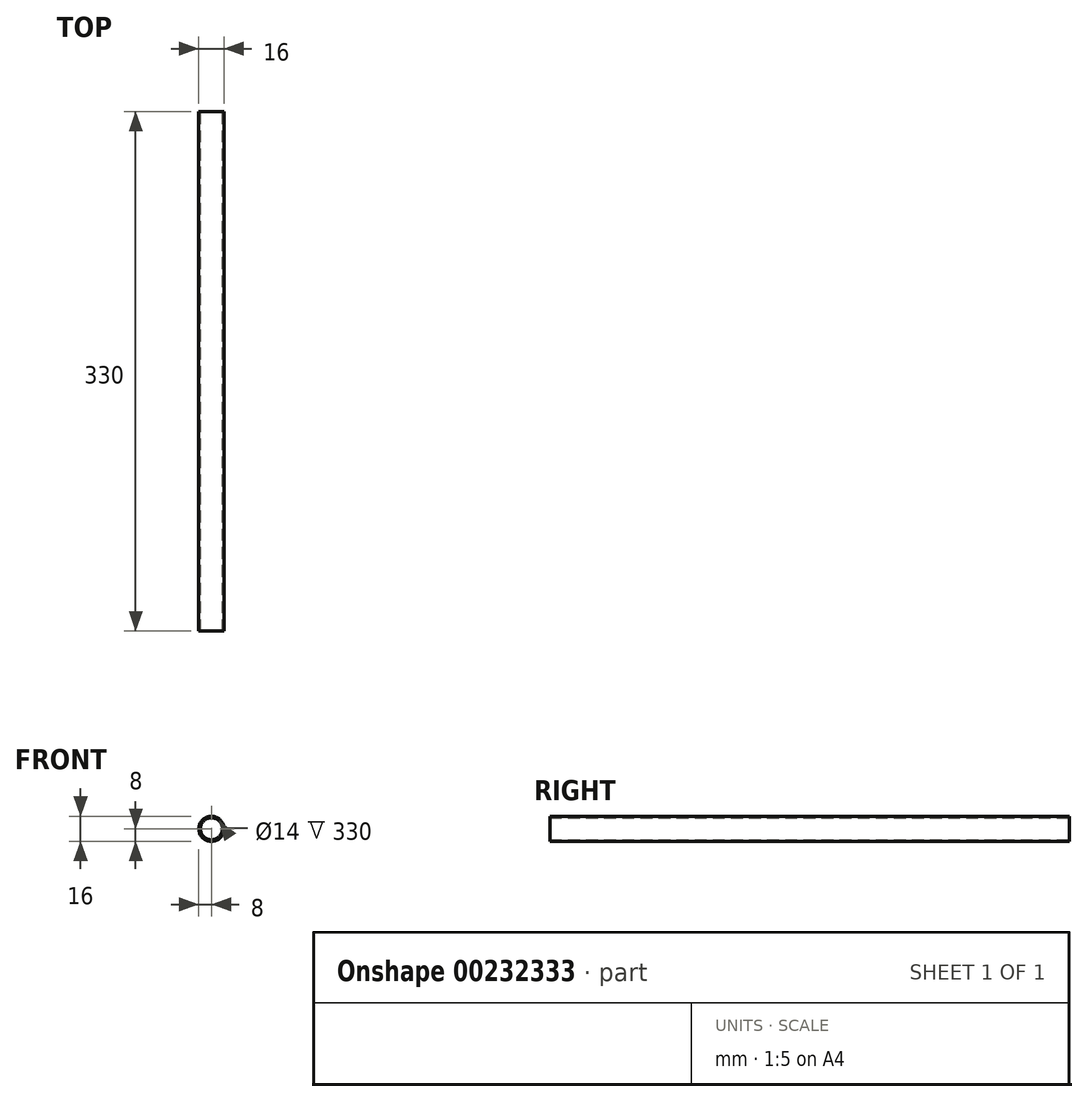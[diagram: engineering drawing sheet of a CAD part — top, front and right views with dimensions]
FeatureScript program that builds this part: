
annotation { "Feature Type Name" : "Feature", "Feature Type Description" : "" }
export const myFeature = defineFeature(function(context is Context, id is Id, definition is map)
    precondition{}
    {
        {
            var Q0;
            Q0=qCreatedBy(makeId("Front.planeOp"),FACE);
            var sketch = newSketch(context, id + "F0", { "sketchPlane" : qUnion([Q0])});
            skCircle(sketch, "E0", {"center": v(0, 0) * mm, "radius": 7 * mm});
            skCircle(sketch, "E1", {"center": v(0, 0) * mm, "radius": 8 * mm});
            skSolve(sketch);
        }
        {
            var Q0;
            Q0=makeQuery(id+"F0.imprint","IMPRINT",FACE,{"disambiguationData":[TD([[makeQuery(id+"F0.imprint","IMPRINT",EDGE,{"derivedFrom":sQuery(id+"F0.wireOp",EDGE,"E0")}),-1.0]])]});
            extrude(context, id + "F1", {"entities" : qUnion([Q0]), "depth" : 330 * mm});
        }
    });
